# Revit family: RN 79000 Optifitt-Serra-Montaggio-Gomito prolungato
name_source: partatom
category: Rohrformteile
units: mm (PartAtom-declared; Revit-internal decimal feet)

## family parameters
Arbeitsebenenbasiert = Nein
Beim Laden mit Abzugskörper schneiden = Nein
Bemaßung runder Anschluss = Durchmesser verwenden
Gemeinsam genutzt = Nein
Immer vertikal = Ja
Teiletyp = Nicht definiert

## types (3) — shared parameters
1.010.00.2 Blattnummer der Richtlinie = 29
1.010.00.3 Ausgabedatum (Monat) der Richtlinie = 201308
1.010.00.4 Herstellername = R. Nussbaum AG
1.010.00.5 Revisionsdatum der Datei = 20190521
1.010.00.6 Webadresse des Herstellers = http://www.nussbaum.ch
1.100.00.4 Produktbezeichnung = Versorgung
1.110.00.2 Index = 3
1.110.00.4 Produktbezeichnung = Optifitt-Serra
1.960/3L.00.8 Link (URL) = https://www.nussbaum.ch
29.700.00.4 Produktname = Optifitt-S-Montage-Anschlusswinkel lang, mit Innengewinde und Arretiervierkant
29.700.00.5 Produktkennung = 2
29.700.00.6 Querschnittsform = 1
29.700.00.7 Nennweitensystem = DN
29.700.00.8 Nenndrucksystem = PN
29.710.02.4 Nenndruck = 16
29.710.02.5 max. zul. Überdruck [hPa] = 1600
29.710.02.7 max. zul. Dauer-Betriebsdruck [hPa] = 1600
29.710.02.9 max. zul. Dauer-Betriebstemperatur [°C] = 95
CONNECTOR0_DIAMETER_dZ_0r = 15 mm
CONNECTOR0_dZ_00 = 30 mm
CONNECTOR0_dZ_01 = 17 mm
CONNECTOR0_ref_dZ = 17 mm
CONNECTOR1_DIAMETER_dX_0r = 15 mm
Connector Visibility = Nein
EnclosingSpace Visibility = Nein
Hersteller = R. Nussbaum AG
URL = https://www.nussbaum.ch

## per-type parameters (varying)
| type | 1.800.00.3 TGA-Nummer | 1.800.00.4 Kommentarfeld | 1.810.00.3 Hersteller-Bestellnummer | 1.810.00.4 DATANORM-Nummer | 1.810.00.5 StLB-Nummer | 1.810.00.6 GTIN-Nummer | 29.710.02.10 Formstück-Gewicht [kg] | 29.710.02.3 Benennung | CONNECTOR1_dX_00 | CONNECTOR1_dX_01 | CONNECTOR1_ref_dX | Modell | R. Nussbaum AG 79000.21 de Visibility | R. Nussbaum AG 79000.22 de Visibility | R. Nussbaum AG 79000.23 de Visibility | Typenkommentare |
| DN=12x15 | 01900300000000000000000000000000000000000000000001???000000000000003 | 79000.23, Optifitt-S-Montage-Anschlusswinkel lang, mit Innengewinde und Arretiervierkant, DN=12x15, L=30, Rp=½ | 79000.23 | 79000.23 | 281.213 | 7612945019509 | 0.437 | Optifitt-S-Montage-Anschlusswinkel lang, mit Innengewinde und Arretiervierkant, DN=12x15, L=30, Rp=½ | 70 mm | 150 mm | 70 mm | 79000.23 | Nein | Nein | Ja | Optifitt-Serra-Montaggio-Gomito prolungato DN=12x15 |
| DN=15 | 01900300000000000000000000000000000000000000000001???000000000000002 | 79000.22, Optifitt-S-Montage-Anschlusswinkel lang, mit Innengewinde und Arretiervierkant, DN=15, L=30, Rp=½ | 79000.22 | 79000.22 | 281.212 | 7612945019493 | 0.306 | Optifitt-S-Montage-Anschlusswinkel lang, mit Innengewinde und Arretiervierkant, DN=15, L=30, Rp=½ | 25 mm  [stored 0.082021 ft] | 90 mm | 25 mm  [stored 0.082021 ft] | 79000.22 | Nein | Ja | Nein | Optifitt-Serra-Montaggio-Gomito prolungato DN=15 |
| DN=1 | 01900300000000000000000000000000000000000000000001???000000000000001 | 79000.21, Optifitt-S-Montage-Anschlusswinkel lang, mit Innengewinde und Arretiervierkant, DN=15, L=30, Rp=½ | 79000.21 | 79000.21 | 281.211 | 7612945019486 | 0.201 | Optifitt-S-Montage-Anschlusswinkel lang, mit Innengewinde und Arretiervierkant, DN=15, L=30, Rp=½ | 10 mm  [stored 0.0328084 ft] | 45 mm | 10 mm  [stored 0.0328084 ft] | 79000.21 | Ja | Nein | Nein | Optifitt-Serra-Montaggio-Gomito prolungato DN=15 |

note: [stored X ft] marks values corroborated as IEEE doubles in the binary element streams (Revit-internal decimal feet)

## geometry (parser evidence)
native form markers: Sweep x2
no freeform markers — native parametric forms only
